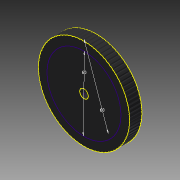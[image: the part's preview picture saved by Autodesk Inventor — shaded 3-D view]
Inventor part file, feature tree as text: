
AUTODESK INVENTOR PART (.ipt)
format: ipt  version: 2014 (Build 180170000, 170)  size: 519,168 bytes
history: native  units: mm
features: sketch x5, extrude x3, pattern_circular x1
ambient origin geometry x8: Origin, YZ Plane, XZ Plane, XY Plane, X Axis, Y Axis, Z Axis, Center Point
bodies: Solid1 (feature_tree)
feature tree (9):
  extrude  "Extrusion1"  Depth=10.0mm TaperAngle=0.0deg
  extrude  "Extrusion2"  Depth=10.0mm TaperAngle=0.0deg
  extrude  "Extrusion3"  Depth=10.0mm TaperAngle=360.0deg
  pattern_circular  "Circular Pattern1"  Count=6  [1 undecoded]
  sketch  "Sketch4"  dims[d13=60.0mm]
  sketch  "Sketch5"
  sketch  "Sketch1"  dims[d0=74.0mm d1=10.0mm d2=0.0mm]
  sketch  "Sketch2"  dims[d3=7.0mm d4=10.0mm d5=0.0mm]
  sketch  "Sketch3"  dims[d7=10.0mm d8=0.0mm d9=800.0mm d10=360.0deg d12=60.0mm]
note: 1 required parameter value undecoded (feature->parameter linkage not recoverable at this tier; creation-order binding heuristic only, values carry confidence <= 0.55)
